# Revit family: EKF_EE_КомплектКронштейновUNIT_PROxima
name_source: partatom
category: Электрооборудование
units: mm (PartAtom-declared; Revit-internal decimal feet)

## family parameters
Всегда вертикально = Нет
На основе рабочей плоскости = Да
Общий = Да
При загрузке вырезать с полостями = Нет
Размер круглого соединителя = Использовать диаметр
Тип детали = Силовой щит
Точка расчета площади = Нет

## types (1)
- Комплект кронштейнов (2шт.) для Din-рейки для ВРУ Unit EKF PROxima
    ADSK_Единица измерения = шт.
    ADSK_Завод-изготовитель = EKF
    ADSK_Код изделия = mb-15-kd
    ADSK_Количество = 1
    ADSK_Марка = Комплект кронштейнов (2шт.)
    ADSK_Масса = 0
    ADSK_Материал = Сталь_Оцинкованная
    ADSK_Наименование = Комплект кронштейнов (2шт.) для Din-рейки для ВРУ Unit EKF PROxima
    ADSK_Обозначение = Комплект кронштейнов (2шт.)
    ADSK_Размер_Высота = 65 мм
    ADSK_Размер_Глубина = 60 мм
    ADSK_Размер_Ширина = 70 мм
    t = 1.2 мм
    Изготовитель = EKF
    Кронштейн_Высота = 65 мм
    Кронштейн_Глубина = 60 мм
    Кронштейн_Ширина = 70 мм
    Отметка по умолчанию = 0 мм
    Серия номенклатуры = Unit PROxima
    Степень защиты IP = -
    ТВ = EKF_2
    Тип = 20 мм
    Тип установки = -
